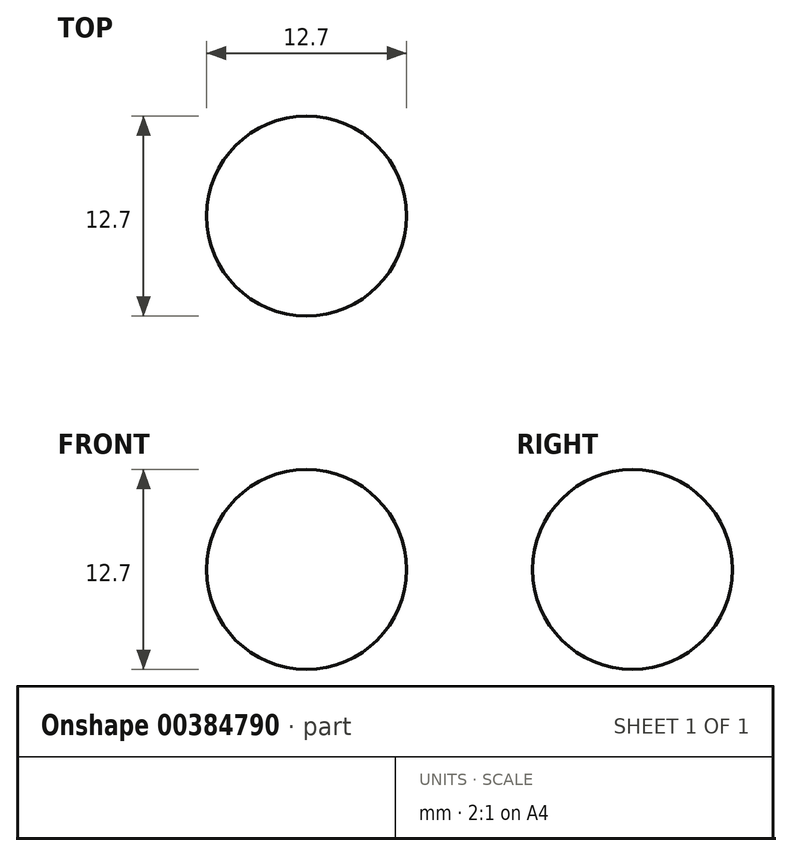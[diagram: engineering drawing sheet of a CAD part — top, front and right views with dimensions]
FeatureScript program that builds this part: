
annotation { "Feature Type Name" : "Feature", "Feature Type Description" : "" }
export const myFeature = defineFeature(function(context is Context, id is Id, definition is map)
    precondition{}
    {
        {
            var Q0;
            Q0=qCreatedBy(makeId("Front.planeOp"),FACE);
            var sketch = newSketch(context, id + "F0", { "sketchPlane" : qUnion([Q0])});
            skLineSegment(sketch, "E0", {"start": v(-52, 16.87) * mm, "end": v(-39.3, 16.87) * mm});
            skArc(sketch, "E1", {"start": v(-39.3, 16.87) * mm, "mid": v(-45.65, 23.22) * mm, "end": v(-52, 16.87) * mm});
            skSolve(sketch);
        }
        {
            var Q0;
            Q0=makeQuery(id+"F0.imprint","IMPRINT",FACE,{"disambiguationData":[TD([[makeQuery(id+"F0.imprint","IMPRINT",EDGE,{"derivedFrom":sQuery(id+"F0.wireOp",EDGE,"E0")}),1.0]])]});
            var Q1;
            Q1=sQuery(id+"F0.wireOp",EDGE,"E0");
            revolve(context, id + "F1", {"entities" : qUnion([Q0]), "axis" : qUnion([Q1]), "revolveType" : RevolveType.FULL});
        }
    });
